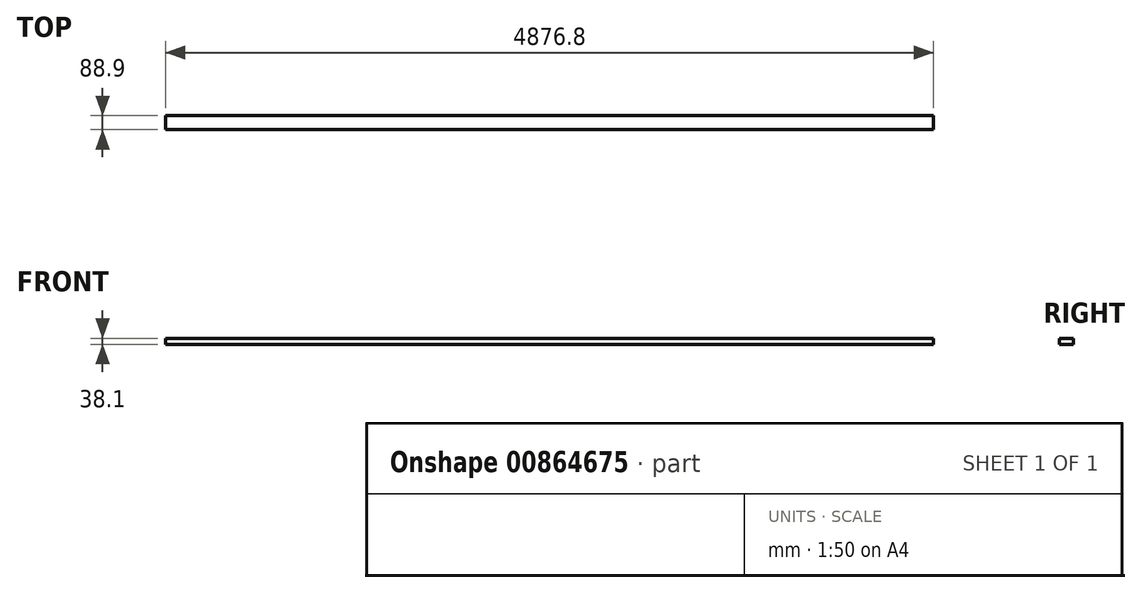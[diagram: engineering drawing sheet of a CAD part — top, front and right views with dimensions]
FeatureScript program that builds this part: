
annotation { "Feature Type Name" : "Feature", "Feature Type Description" : "" }
export const myFeature = defineFeature(function(context is Context, id is Id, definition is map)
    precondition{}
    {
        {
            var Q0;
            Q0=qCreatedBy(makeId("Right.planeOp"),FACE);
            var sketch = newSketch(context, id + "F0", { "sketchPlane" : qUnion([Q0])});
            skLineSegment(sketch, "E0", {"start": v(0, 0) * mm, "end": v(88.9, 0) * mm});
            skLineSegment(sketch, "E1", {"start": v(88.9, 0) * mm, "end": v(88.9, 38.1) * mm});
            skLineSegment(sketch, "E2", {"start": v(88.9, 38.1) * mm, "end": v(0, 38.1) * mm});
            skLineSegment(sketch, "E3", {"start": v(0, 38.1) * mm, "end": v(0, 0) * mm});
            skSolve(sketch);
        }
        {
            var Q0;
            Q0=makeQuery(id+"F0.imprint","IMPRINT",FACE,{"disambiguationData":[TD([[makeQuery(id+"F0.imprint","IMPRINT",EDGE,{"derivedFrom":sQuery(id+"F0.wireOp",EDGE,"E0")}),1.0]])]});
            extrude(context, id + "F1", {"entities" : qUnion([Q0]), "depth" : 4876.8 * mm, "offsetDistance" : 25.4 * mm});
        }
    });
